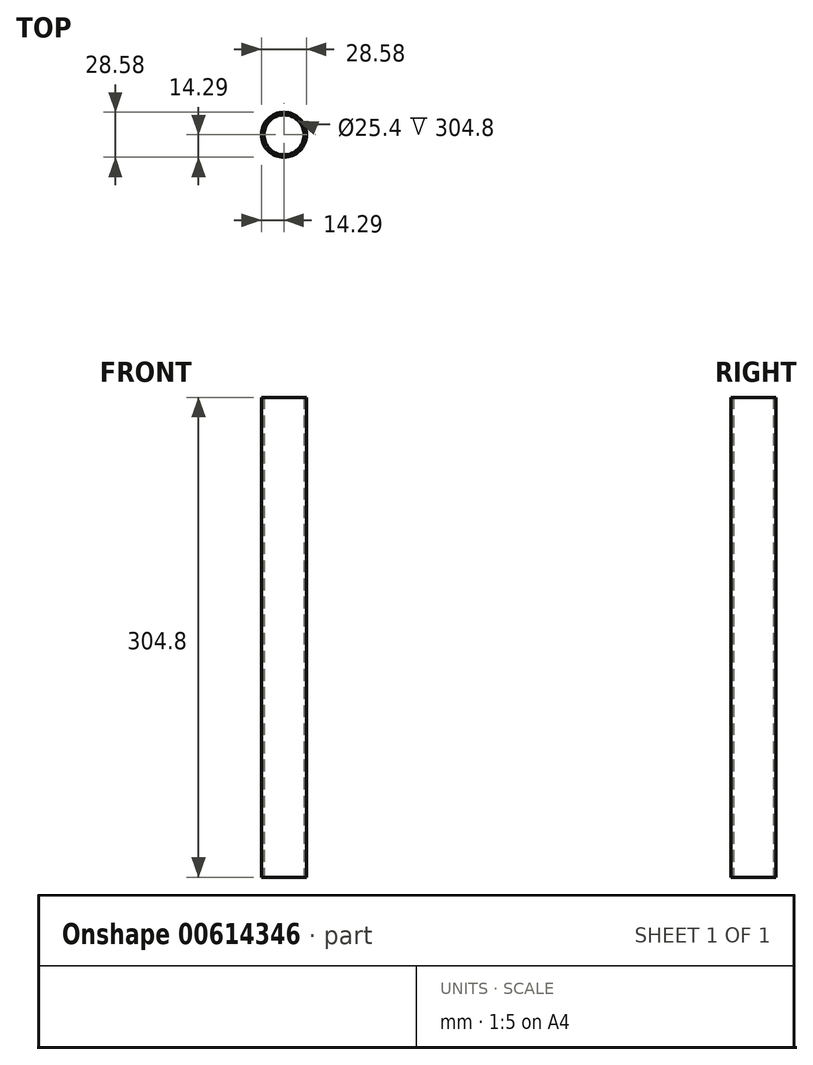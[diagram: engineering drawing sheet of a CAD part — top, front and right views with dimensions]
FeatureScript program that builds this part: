
annotation { "Feature Type Name" : "Feature", "Feature Type Description" : "" }
export const myFeature = defineFeature(function(context is Context, id is Id, definition is map)
    precondition{}
    {
        {
            var Q0;
            Q0=qCreatedBy(makeId("Top.planeOp"),FACE);
            var sketch = newSketch(context, id + "F0", { "sketchPlane" : qUnion([Q0])});
            skLineSegment(sketch, "E0", {"start": v(0, 0) * mm, "end": v(12.7, 0) * mm});
            skCircle(sketch, "E1", {"center": v(0, 0) * mm, "radius": 12.7 * mm});
            skCircle(sketch, "E2.0", {"center": v(0, 0) * mm, "radius": 14.29 * mm});
            skSolve(sketch);
        }
        {
            var Q0;
            Q0=qSketchRegion(id+"FEloJnSHgHgsXCt_0",true);
            var Q1;
            Q1=makeQuery(id+"F0.imprint","IMPRINT",FACE,{"disambiguationData":[TD([[makeQuery(id+"F0.imprint","IMPRINT",EDGE,{"derivedFrom":sQuery(id+"F0.wireOp",EDGE,"E1")}),-1.0]])]});
            extrude(context, id + "F1", {"entities" : qUnion([Q0, Q1]), "depth" : 304.8 * mm, "offsetDistance" : 25.4 * mm});
        }
    });
